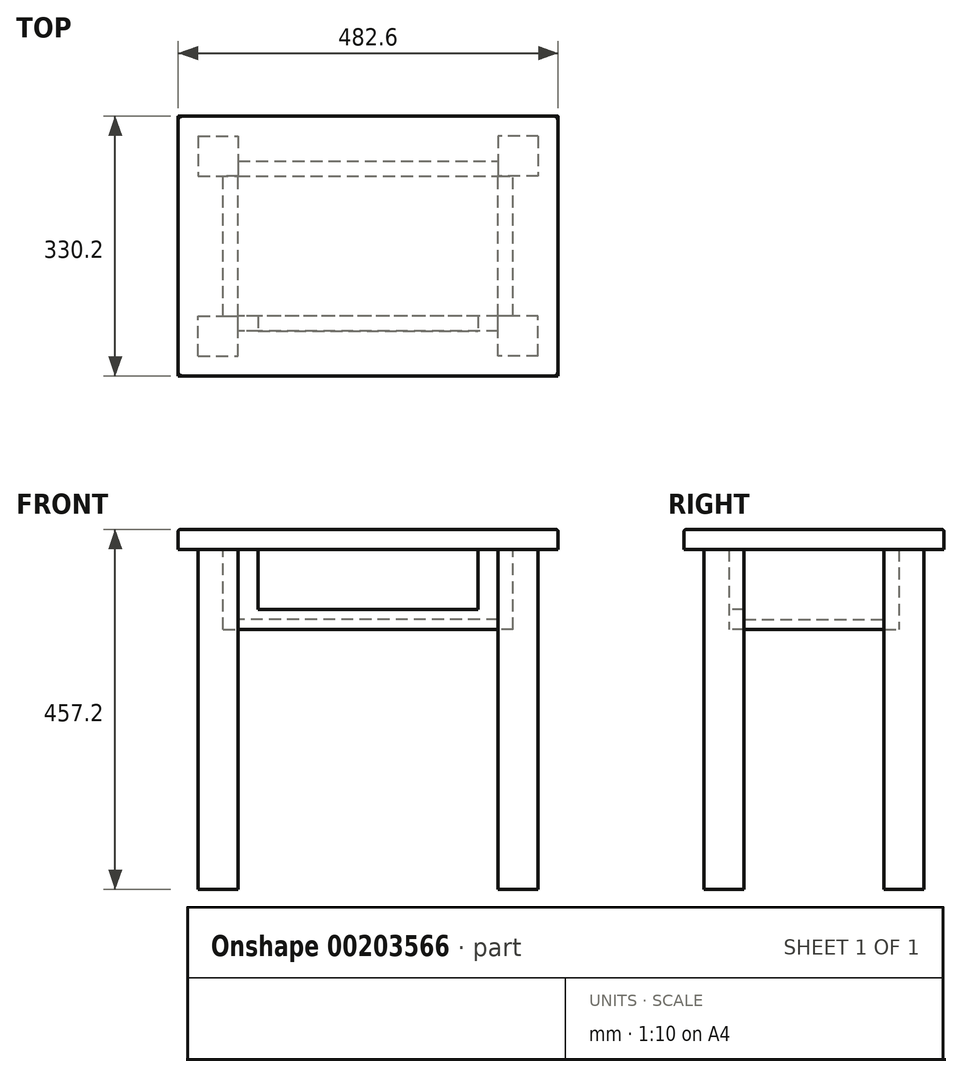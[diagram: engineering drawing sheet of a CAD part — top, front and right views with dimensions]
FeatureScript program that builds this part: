
annotation { "Feature Type Name" : "Feature", "Feature Type Description" : "" }
export const myFeature = defineFeature(function(context is Context, id is Id, definition is map)
    precondition{}
    {
        {
            var Q0;
            Q0=qCreatedBy(makeId("Top.planeOp"),FACE);
            var sketch = newSketch(context, id + "F0", { "sketchPlane" : qUnion([Q0])});
            skLineSegment(sketch, "E0.bottom", {"start": v(241.3, 165.1) * mm, "end": v(-241.3, 165.1) * mm});
            skLineSegment(sketch, "E0.top", {"start": v(241.3, -165.1) * mm, "end": v(-241.3, -165.1) * mm});
            skLineSegment(sketch, "E0.left", {"start": v(241.3, 165.1) * mm, "end": v(241.3, -165.1) * mm});
            skLineSegment(sketch, "E0.right", {"start": v(-241.3, 165.1) * mm, "end": v(-241.3, -165.1) * mm});
            skPoint(sketch, "E0.middle", {"position": v(0, 0) * mm});
            skSolve(sketch);
        }
        {
            var Q0;
            Q0=makeQuery(id+"F0.imprint","IMPRINT",FACE,{"disambiguationData":[TD([[makeQuery(id+"F0.imprint","IMPRINT",EDGE,{"derivedFrom":sQuery(id+"F0.wireOp",EDGE,"E0.bottom")}),1.0]])]});
            extrude(context, id + "F1", {"entities" : qUnion([Q0]), "depth" : 25.4 * mm});
        }
        {
            var Q0;
            Q0=makeQuery(id+"F1.opExtrude","CAP_FACE",FACE,{"disambiguationData":[OSD([sQuery(id+"F0.wireOp",EDGE,"E0.bottom"),sQuery(id+"F0.wireOp",EDGE,"E0.top"),sQuery(id+"F0.wireOp",EDGE,"E0.left"),sQuery(id+"F0.wireOp",EDGE,"E0.right")])],"isStart":false});
            fillet(context, id + "F2", {"entities" : qUnion([Q0]), "radius" : 2.54 * mm, "tangentPropagation" : true, "allowEdgeOverflow" : false});
        }
        {
            var Q0;
            Q0=makeQuery(id+"F1.opExtrude","CAP_FACE",FACE,{"disambiguationData":[OSD([sQuery(id+"F0.wireOp",EDGE,"E0.bottom"),sQuery(id+"F0.wireOp",EDGE,"E0.top"),sQuery(id+"F0.wireOp",EDGE,"E0.left"),sQuery(id+"F0.wireOp",EDGE,"E0.right")])],"isStart":true});
            var sketch = newSketch(context, id + "F3", { "sketchPlane" : qUnion([Q0])});
            skLineSegment(sketch, "E1.bottom", {"start": v(215.9, 139.7) * mm, "end": v(165.1, 139.7) * mm});
            skLineSegment(sketch, "E1.top", {"start": v(215.9, 88.9) * mm, "end": v(165.1, 88.9) * mm});
            skLineSegment(sketch, "E1.left", {"start": v(215.9, 139.7) * mm, "end": v(215.9, 88.9) * mm});
            skLineSegment(sketch, "E1.right", {"start": v(165.1, 139.7) * mm, "end": v(165.1, 88.9) * mm});
            skSolve(sketch);
        }
        {
            var Q0;
            Q0=makeQuery(id+"F3.imprint","IMPRINT",FACE,{"disambiguationData":[TD([[makeQuery(id+"F3.imprint","IMPRINT",EDGE,{"derivedFrom":sQuery(id+"F3.wireOp",EDGE,"E1.bottom")}),1.0]])]});
            extrude(context, id + "F4", {"entities" : qUnion([Q0]), "depth" : 431.8 * mm});
        }
        {
            var Q0;
            Q0=makeQuery(id+"F4.opExtrude","SWEPT_BODY",BODY,{"disambiguationData":[OSD([sQuery(id+"F3.wireOp",EDGE,"E1.bottom"),sQuery(id+"F3.wireOp",EDGE,"E1.top"),sQuery(id+"F3.wireOp",EDGE,"E1.left"),sQuery(id+"F3.wireOp",EDGE,"E1.right")])]});
            var Q1;
            Q1=qCreatedBy(makeId("Right.planeOp"),FACE);
            mirror(context, id + "F5", {"entities" : qUnion([Q0]), "mirrorPlane" : qUnion([Q1])});
        }
        {
            var Q0;
            Q0=makeQuery(id+"F4.opExtrude","SWEPT_BODY",BODY,{"disambiguationData":[OSD([sQuery(id+"F3.wireOp",EDGE,"E1.bottom"),sQuery(id+"F3.wireOp",EDGE,"E1.top"),sQuery(id+"F3.wireOp",EDGE,"E1.left"),sQuery(id+"F3.wireOp",EDGE,"E1.right")])]});
            var Q1;
            Q1=makeQuery(id+"F5.opPattern","COPY",BODY,{"derivedFrom":makeQuery(id+"F4.opExtrude","SWEPT_BODY",BODY,{"disambiguationData":[OSD([sQuery(id+"F3.wireOp",EDGE,"E1.bottom"),sQuery(id+"F3.wireOp",EDGE,"E1.top"),sQuery(id+"F3.wireOp",EDGE,"E1.left"),sQuery(id+"F3.wireOp",EDGE,"E1.right")])]}),"instanceName":"1"});
            var Q2;
            Q2=qCreatedBy(makeId("Front.planeOp"),FACE);
            mirror(context, id + "F6", {"entities" : qUnion([Q0, Q1]), "mirrorPlane" : qUnion([Q2])});
        }
        {
            var Q0;
            Q0=makeQuery(id+"F5.opPattern","COPY",FACE,{"derivedFrom":makeQuery(id+"F4.opExtrude","SWEPT_FACE",FACE,{"disambiguationData":[OSD([sQuery(id+"F3.wireOp",EDGE,"E1.right")])]}),"instanceName":"1"});
            var sketch = newSketch(context, id + "F7", { "sketchPlane" : qUnion([Q0])});
            skLineSegment(sketch, "E2.bottom", {"start": v(-88.9, 0) * mm, "end": v(-107.95, 0) * mm});
            skLineSegment(sketch, "E2.top", {"start": v(-88.9, -101.6) * mm, "end": v(-107.95, -101.6) * mm});
            skLineSegment(sketch, "E2.left", {"start": v(-88.9, 0) * mm, "end": v(-88.9, -101.6) * mm});
            skLineSegment(sketch, "E2.right", {"start": v(-107.95, 0) * mm, "end": v(-107.95, -101.6) * mm});
            skSolve(sketch);
        }
        {
            var Q0;
            Q0 = qSketchRegion(id + "F7", true);
            extrude(context, id + "F8", {"entities" : qUnion([Q0]), "endBound" : BoundingType.UP_TO_NEXT, "depth" : 8.9 * mm});
        }
        {
            var Q0;
            Q0=makeQuery(id+"F6.opPattern","COPY",FACE,{"derivedFrom":makeQuery(id+"F5.opPattern","COPY",FACE,{"derivedFrom":makeQuery(id+"F4.opExtrude","SWEPT_FACE",FACE,{"disambiguationData":[OSD([sQuery(id+"F3.wireOp",EDGE,"E1.top")])]}),"instanceName":"1"}),"instanceName":"1"});
            var sketch = newSketch(context, id + "F9", { "sketchPlane" : qUnion([Q0])});
            skLineSegment(sketch, "E3.bottom", {"start": v(-165.1, 0) * mm, "end": v(-184.15, 0) * mm});
            skLineSegment(sketch, "E3.top", {"start": v(-165.1, -101.6) * mm, "end": v(-184.15, -101.6) * mm});
            skLineSegment(sketch, "E3.left", {"start": v(-165.1, 0) * mm, "end": v(-165.1, -101.6) * mm});
            skLineSegment(sketch, "E3.right", {"start": v(-184.15, 0) * mm, "end": v(-184.15, -101.6) * mm});
            skSolve(sketch);
        }
        {
            var Q0;
            Q0=makeQuery(id+"F9.imprint","IMPRINT",FACE,{"disambiguationData":[TD([[makeQuery(id+"F9.imprint","IMPRINT",EDGE,{"derivedFrom":sQuery(id+"F9.wireOp",EDGE,"E3.bottom")}),-1.0]])]});
            extrude(context, id + "F10", {"entities" : qUnion([Q0]), "endBound" : BoundingType.UP_TO_NEXT, "depth" : 25.4 * mm});
        }
        {
            var Q0;
            Q0=makeQuery(id+"F10.opExtrude","SWEPT_BODY",BODY,{"disambiguationData":[OSD([sQuery(id+"F9.wireOp",EDGE,"E3.bottom"),sQuery(id+"F9.wireOp",EDGE,"E3.top"),sQuery(id+"F9.wireOp",EDGE,"E3.left"),sQuery(id+"F9.wireOp",EDGE,"E3.right")])]});
            var Q1;
            Q1=qCreatedBy(makeId("Right.planeOp"),FACE);
            mirror(context, id + "F11", {"entities" : qUnion([Q0]), "mirrorPlane" : qUnion([Q1])});
        }
        {
            var Q0;
            Q0=makeQuery(id+"F6.opPattern","COPY",FACE,{"derivedFrom":makeQuery(id+"F4.opExtrude","SWEPT_FACE",FACE,{"disambiguationData":[OSD([sQuery(id+"F3.wireOp",EDGE,"E1.right")])]}),"instanceName":"1"});
            var sketch = newSketch(context, id + "F12", { "sketchPlane" : qUnion([Q0])});
            skLineSegment(sketch, "E4.bottom", {"start": v(-88.9, 0) * mm, "end": v(-107.95, 0) * mm});
            skLineSegment(sketch, "E4.top", {"start": v(-88.9, -101.6) * mm, "end": v(-107.95, -101.6) * mm});
            skLineSegment(sketch, "E4.left", {"start": v(-88.9, 0) * mm, "end": v(-88.9, -101.6) * mm});
            skLineSegment(sketch, "E4.right", {"start": v(-107.95, 0) * mm, "end": v(-107.95, -101.6) * mm});
            skSolve(sketch);
        }
        {
            var Q0;
            Q0=makeQuery(id+"F12.imprint","IMPRINT",FACE,{"disambiguationData":[TD([[makeQuery(id+"F12.imprint","IMPRINT",EDGE,{"derivedFrom":sQuery(id+"F12.wireOp",EDGE,"E4.bottom")}),-1.0]])]});
            extrude(context, id + "F13", {"entities" : qUnion([Q0]), "endBound" : BoundingType.UP_TO_NEXT, "depth" : 25.4 * mm});
        }
        {
            var Q0;
            Q0=makeQuery(id+"F8.opExtrude","SWEPT_FACE",FACE,{"disambiguationData":[OSD([sQuery(id+"F7.wireOp",EDGE,"E2.top")])]});
            var sketch = newSketch(context, id + "F14", { "sketchPlane" : qUnion([Q0])});
            skLineSegment(sketch, "E5.0", {"start": v(165.1, 88.9) * mm, "end": v(165.1, -88.9) * mm});
            skLineSegment(sketch, "E6.0", {"start": v(-165.1, -88.9) * mm, "end": v(165.1, -88.9) * mm});
            skLineSegment(sketch, "E7.0", {"start": v(165.1, 88.9) * mm, "end": v(-165.1, 88.9) * mm});
            skLineSegment(sketch, "E8.0", {"start": v(-165.1, 88.9) * mm, "end": v(-165.1, -88.9) * mm});
            skSolve(sketch);
        }
        {
            var Q0;
            Q0=makeQuery(id+"F14.imprint","IMPRINT",FACE,{"disambiguationData":[TD([[makeQuery(id+"F14.imprint","IMPRINT",EDGE,{"derivedFrom":sQuery(id+"F14.wireOp",EDGE,"E5.0")}),-1.0]])]});
            extrude(context, id + "F15", {"entities" : qUnion([Q0]), "oppositeDirection" : true, "depth" : 12.7 * mm});
        }
        {
            var Q0;
            Q0=makeQuery(id+"F8.opExtrude","SWEPT_FACE",FACE,{"disambiguationData":[OSD([sQuery(id+"F7.wireOp",EDGE,"E2.right")])]});
            var sketch = newSketch(context, id + "F16", { "sketchPlane" : qUnion([Q0])});
            skLineSegment(sketch, "E9.bottom", {"start": v(-139.7, 0) * mm, "end": v(139.7, 0) * mm});
            skLineSegment(sketch, "E9.top", {"start": v(-139.7, -76.2) * mm, "end": v(139.7, -76.2) * mm});
            skLineSegment(sketch, "E9.left", {"start": v(-139.7, 0) * mm, "end": v(-139.7, -76.2) * mm});
            skLineSegment(sketch, "E9.right", {"start": v(139.7, 0) * mm, "end": v(139.7, -76.2) * mm});
            skSolve(sketch);
        }
        {
            var Q0;
            Q0=makeQuery(id+"F16.imprint","IMPRINT",FACE,{"disambiguationData":[TD([[makeQuery(id+"F16.imprint","IMPRINT",EDGE,{"derivedFrom":sQuery(id+"F16.wireOp",EDGE,"E9.bottom")}),1.0]])]});
            extrude(context, id + "F17", {"entities" : qUnion([Q0]), "operationType" : NewBodyOperationType.REMOVE, "endBound" : BoundingType.UP_TO_NEXT, "oppositeDirection" : true, "depth" : 25.4 * mm});
        }
    });
